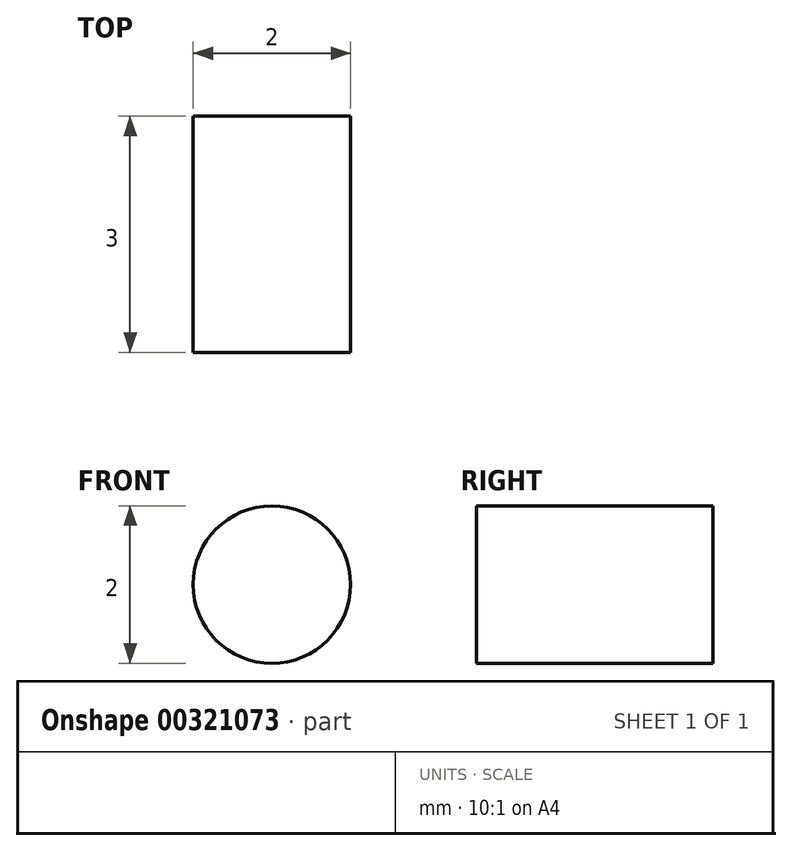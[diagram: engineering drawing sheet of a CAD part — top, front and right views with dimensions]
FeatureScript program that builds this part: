
annotation { "Feature Type Name" : "Feature", "Feature Type Description" : "" }
export const myFeature = defineFeature(function(context is Context, id is Id, definition is map)
    precondition{}
    {
        {
            var Q0;
            Q0=qCreatedBy(makeId("Front.planeOp"),FACE);
            var sketch = newSketch(context, id + "F0", { "sketchPlane" : qUnion([Q0])});
            skCircle(sketch, "E0", {"center": v(0, 0) * mm, "radius": 1 * mm});
            skSolve(sketch);
        }
        {
            var Q0;
            Q0 = qSketchRegion(id + "F0", true);
            extrude(context, id + "F1", {"entities" : qUnion([Q0]), "depth" : 3 * mm});
        }
    });
